# Revit family: Shower-Valve_Trim-KOHLER-MODULO-K-99967T
name_source: partatom
category: Plumbing Fixtures
revit_build: Autodesk Revit 2017 (Build: 20160225_1515(x64)
units: mm (PartAtom-declared; Revit-internal decimal feet)

## family parameters
Cut with Voids When Loaded = No
Host = Face
OmniClass Number = 23.31.25.00
OmniClass Title = Toilet and Bath Specialties
Part Type = Normal
Room Calculation Point = No
Round Connector Dimension = Use Diameter
Shared = No

## types (4) — shared parameters
ADA Compliant = No
Assembly Code = D2010700
CW Connection = Yes
Cold Water Inlet = Cold Water Inlet
Date Modified = 09/28/2020
Default Elevation = 42"
Drain Included = No
Flow Rate = 0 GPM
HW Connection = Yes
Height = 7 1/16"
Hot Water Inlet = Hot Water Inlet
Manufacturer = KOHLER Co.
Master Format 2014 = 22 42 23
Master Format 2014 Name = Residential Showers
Material = Premium Metal Construction
Panel Thickness = 0"
Pressure = 72.51 psi
Product Documentation Link = https://files.kohler.com.cn
Product Name = MODULO
Product Page URL = https://www.kohler.com.cn
Tempered Water Outlet 1 = Tempered Water Outlet 1
Tempered Water Outlet 2 = Tempered Water Outlet 2
URL = http://www.kohler.com.cn
Vent Connection = No
Waste Connection = No
Waste Water Outlet = Waste Water Outlet
WaterSense Certified = No
Width = 5 1/2"

## per-type parameters (varying)
| type | Description | Finish | Length | Mema Cross Handle | Mema Lever Handle | Model | Type |
| Mema Cross Handle, CP- Polished Chrome | Smart Formula-Shaped in Wall-thermostatic Shower Valve Core And Panel- Classic type(Mema Cross Handle) | Kohler-Metal-CP-Polished_Chrome | 4 1/8" | Yes | No | K-99967T-3S-CP | 1 |
| Mema Cross Handle, BL- Matte Black | Smart Formula-Shaped in Wall-thermostatic Shower Valve Core And Panel- Classic type(Mema Cross Handle) | Kohler-Metal-BL-Matte_Black | 4 1/8" | Yes | No | K-99967T-3S -BL | 2 |
| Mema Lever Handle, CP- Polished Chrome | Smart Formula-Shaped in Wall-thermostatic Shower Valve Core And Panel- Classic type(Mema Lever Handle) | Kohler-Metal-CP-Polished_Chrome | 4 1/4" | No | Yes | K-99967T-4V-CP | 3 |
| Mema Lever Handle, BL- Matte Black | Smart Formula-Shaped in Wall-thermostatic Shower Valve Core And Panel- Classic type(Mema Lever Handle) | Kohler-Metal-BL-Matte_Black | 4 1/4" | No | Yes | K-99967T-4V-BL | 4 |

## geometry (parser evidence)
native form markers: Sweep x10
no freeform markers — native parametric forms only
